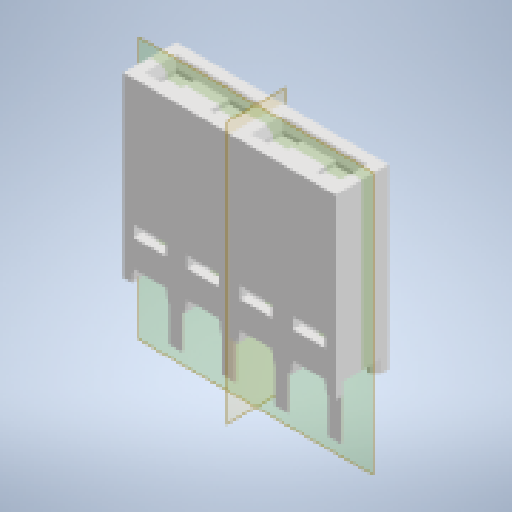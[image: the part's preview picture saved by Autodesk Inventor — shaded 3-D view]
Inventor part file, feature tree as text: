
AUTODESK INVENTOR PART (.ipt)
format: ipt  version: 2023.2 (Build 272271000, 271)  size: 351,232 bytes
history: native  units: in
note: dims shown in document units (in); Inventor stores cm internally (conversion verified against a paired STEP export)
features: plane x2, other x1, sketch x1, imported_body x1
ambient origin geometry x8: Origin, YZ Plane, XZ Plane, XY Plane, X Axis, Y Axis, Z Axis, Center Point
bodies: Solid1 (feature_tree)
feature tree (5):
  other  "Repaired Geometry1"
  plane  "Work Plane1"
  plane  "Work Plane2"
  sketch  "3D Sketch1"
  imported_body  "Base1"
